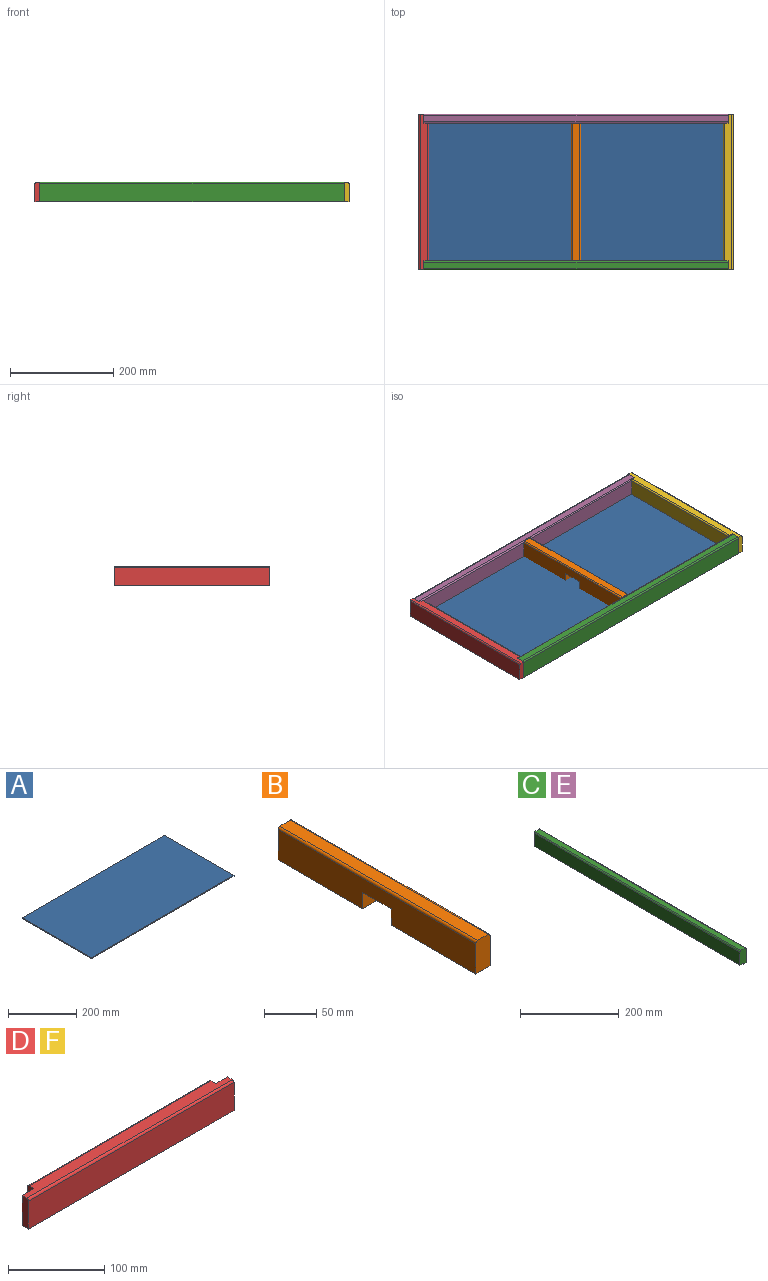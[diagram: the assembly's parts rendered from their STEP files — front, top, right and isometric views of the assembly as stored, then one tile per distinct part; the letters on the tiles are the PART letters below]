
ASSEMBLY  parts=6 mates=5
PART A: 6 faces, bbox 590.6x285.8x3.2 mm
  f0: plane 590.55x3.18mm, normal (0,-1,0), area 1875mm2, adj f1,f3,f4,f5
  f1: plane 285.75x3.18mm, normal (1,0,0), area 907.3mm2, adj f0,f2,f4,f5
  f2: plane 590.55x3.18mm, normal (0,1,0), area 1875mm2, adj f1,f3,f4,f5
  f3: plane 285.75x3.18mm, normal (-1,0,0), area 907.3mm2, adj f0,f2,f4,f5
  f4: plane 590.55x285.75mm, normal (0,0,1), area 168749.7mm2, adj f0,f1,f2,f3
  f5: plane 590.55x285.75mm, normal (0,0,-1), area 168749.7mm2, adj f0,f1,f2,f3
PART B: 12 faces, bbox 19.1x266.7x38.1 mm
  f0: plane 114.3x19.05mm, normal (0,0,-1), area 2177.4mm2, adj f1,f2,f3,f9
  f1: plane 266.7x35.56mm, normal (1,0,0), area 8758mm2, adj f0,f3,f4,f6,f7,f9,f10,f11
  f2: plane 266.7x35.56mm, normal (-1,0,0), area 8758mm2, adj f0,f3,f4,f6,f8,f9,f10,f11
  f3: plane 38.1x19.05mm, normal (0,-1,0), area 723mm2, adj f0,f1,f2,f5,f7,f8
  f4: plane 38.1x19.05mm, normal (0,1,0), area 723mm2, adj f1,f2,f5,f6,f7,f8
  f5: plane 266.7x13.97mm, normal (0,0,1), area 3725.8mm2, adj f3,f4,f7,f8
  f6: plane 114.3x19.05mm, normal (0,0,-1), area 2177.4mm2, adj f1,f2,f4,f10
  f7: cylinder r=2.54mm len=266.7mm, axis (0,-1,0), area 1064.1mm2, adj f1,f3,f4,f5
  f8: cylinder r=2.54mm len=266.7mm, axis (0,1,0), area 1064.1mm2, adj f2,f3,f4,f5
  f9: plane 19.05x19.05mm, normal (0,1,0), area 362.9mm2, adj f0,f1,f2,f11
  f10: plane 19.05x19.05mm, normal (0,-1,0), area 362.9mm2, adj f1,f2,f6,f11
  f11: plane 38.1x19.05mm, normal (0,0,-1), area 725.8mm2, adj f1,f2,f9,f10
PART C: 10 faces, bbox 17.5x590.6x38.1 mm
  f0: plane 590.55x32.39mm, normal (-1,0,0), area 19125mm2, adj f1,f7,f8,f9
  f1: plane 590.55x9.53mm, normal (0,0,-1), area 5625mm2, adj f0,f2,f8,f9
  f2: plane 590.55x3.18mm, normal (-1,0,0), area 1875mm2, adj f1,f3,f8,f9
  f3: plane 590.55x7.94mm, normal (0,0,-1), area 4687.5mm2, adj f2,f4,f8,f9
  f4: plane 590.55x35.56mm, normal (1,0,0), area 21000mm2, adj f3,f5,f8,f9
  f5: cylinder r=2.54mm len=590.55mm, axis (0,1,0), area 2356.2mm2, adj f4,f6,f8,f9
  f6: plane 590.55x12.38mm, normal (0,0,1), area 7312.5mm2, adj f5,f7,f8,f9
  f7: cylinder r=2.54mm len=590.55mm, axis (0,1,0), area 2356.2mm2, adj f0,f6,f8,f9
  f8: plane 38.1x17.46mm, normal (0,-1,0), area 632.3mm2, adj f0,f1,f2,f3,f4,f5,f6,f7
  f9: plane 38.1x17.46mm, normal (0,1,0), area 632.3mm2, adj f0,f1,f2,f3,f4,f5,f6,f7
PART D: 12 faces, bbox 301.6x19.1x38.1 mm
  f0: plane 34.93x9.53mm, normal (-1,0,0), area 331.3mm2, adj f4,f6,f7,f10,f11
  f1: plane 38.1x9.53mm, normal (-1,0,0), area 361.5mm2, adj f2,f4,f7,f8,f9
  f2: plane 301.63x35.56mm, normal (0,-1,0), area 10725.8mm2, adj f1,f3,f8,f9
  f3: plane 38.1x9.53mm, normal (1,0,0), area 361.5mm2, adj f2,f4,f7,f8,f9
  f4: plane 301.63x38.1mm, normal (0,1,0), area 2177.4mm2, adj f0,f1,f3,f5,f7,f8,f11
  f5: plane 34.93x9.53mm, normal (1,0,0), area 331.3mm2, adj f4,f6,f7,f10,f11
  f6: plane 266.7x32.39mm, normal (0,1,0), area 8637.1mm2, adj f0,f5,f10,f11
  f7: plane 301.63x13.97mm, normal (0,0,1), area 3969.8mm2, adj f0,f1,f3,f4,f5,f9,f10
  f8: plane 301.63x9.53mm, normal (0,0,-1), area 2873mm2, adj f1,f2,f3,f4
  f9: cylinder r=2.54mm len=301.63mm, axis (-1,0,0), area 1203.4mm2, adj f1,f2,f3,f7
  f10: cylinder r=2.54mm len=266.7mm, axis (1,0,0), area 1064.1mm2, adj f0,f5,f6,f7
  f11: plane 266.7x9.53mm, normal (0,0,-1), area 2540.3mm2, adj f0,f4,f5,f6
PART E: same geometry as C
PART F: same geometry as D
PLACE A t=(-25.02,80.93,9.9)mm fixed
PLACE B t=(-25.02,80.93,10.29)mm
PLACE C rot(axis=(0,0,-1),90deg) t=(270.25,-61.95,30.22)mm fixed
PLACE D rot(axis=(0,0,-1),90deg) t=(-320.3,214.28,9.9)mm fixed
PLACE E rot(axis=(0,0,1),90deg) t=(-320.3,223.8,30.22)mm
PLACE F rot(axis=(0,0,1),90deg) t=(270.25,-52.42,9.9)mm
MATE fastened F.f4 <-> A.f1  axis (-1,0,0) through (270.25,80.93,9.9)mm
MATE fastened B.f4 <-> E.f0  axis (0,1,0) through (-25.02,214.28,29.27)mm
MATE fastened A.f0 <-> C.f2  axis (0,-1,0) through (-25.02,-61.95,11.49)mm
MATE fastened E.f1 <-> A.f4  axis (0,0,-1) through (-25.02,223.8,13.07)mm
MATE fastened D.f11 <-> A.f4  axis (0,0,-1) through (-320.3,80.93,13.07)mm
